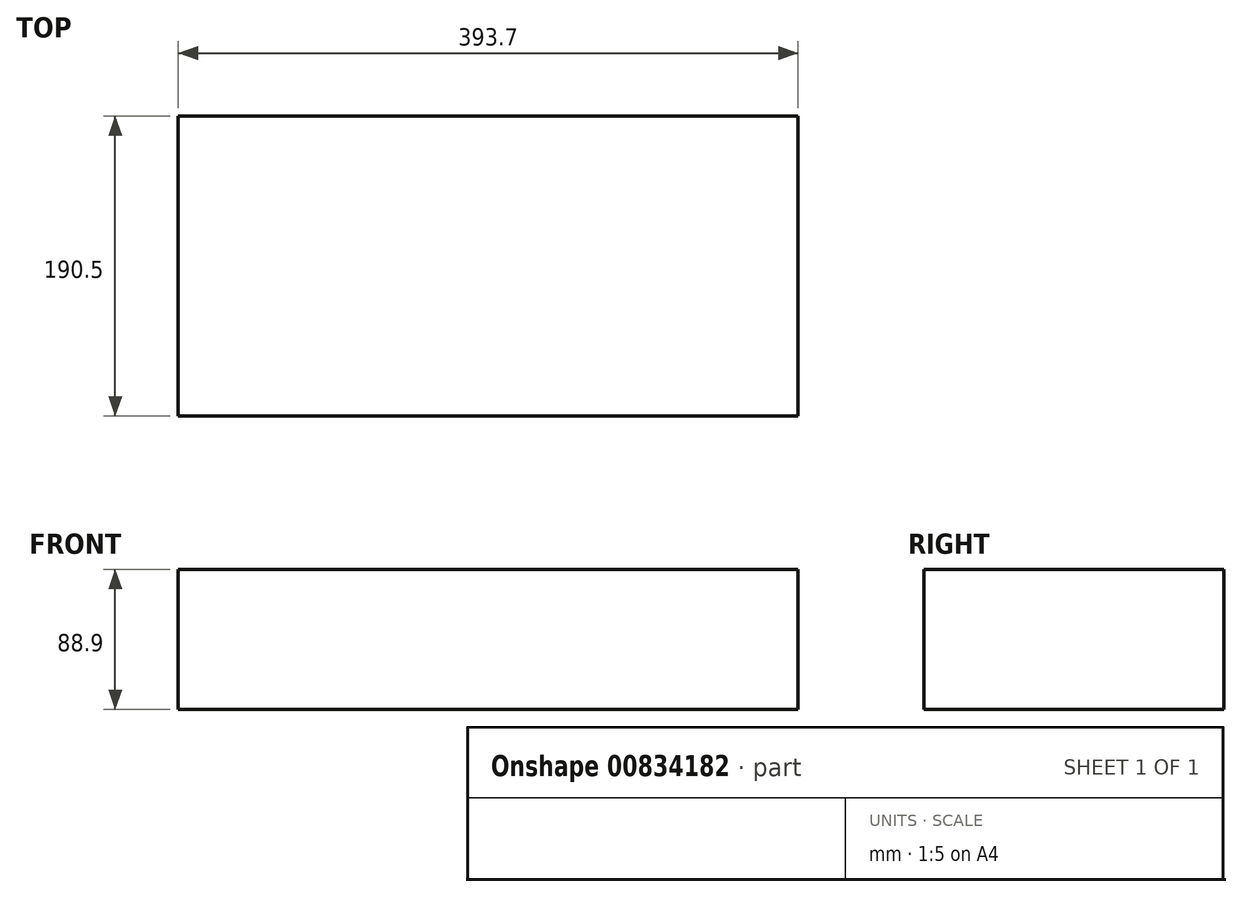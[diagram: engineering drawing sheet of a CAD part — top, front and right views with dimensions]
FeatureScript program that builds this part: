
annotation { "Feature Type Name" : "Feature", "Feature Type Description" : "" }
export const myFeature = defineFeature(function(context is Context, id is Id, definition is map)
    precondition{}
    {
        {
            var Q0;
            Q0=qCreatedBy(makeId("Top.planeOp"),FACE);
            var sketch = newSketch(context, id + "F0", { "sketchPlane" : qUnion([Q0])});
            skLineSegment(sketch, "E0.bottom", {"start": v(-196.85, 95.25) * mm, "end": v(196.85, 95.25) * mm});
            skLineSegment(sketch, "E0.top", {"start": v(-196.85, -95.25) * mm, "end": v(196.85, -95.25) * mm});
            skLineSegment(sketch, "E0.left", {"start": v(-196.85, 95.25) * mm, "end": v(-196.85, -95.25) * mm});
            skLineSegment(sketch, "E0.right", {"start": v(196.85, 95.25) * mm, "end": v(196.85, -95.25) * mm});
            skPoint(sketch, "E0.middle", {"position": v(0, 0) * mm});
            skSolve(sketch);
        }
        {
            var Q0;
            Q0=makeQuery(id+"F0.imprint","IMPRINT",FACE,{"disambiguationData":[TD([[makeQuery(id+"F0.imprint","IMPRINT",EDGE,{"derivedFrom":sQuery(id+"F0.wireOp",EDGE,"E0.bottom")}),-1.0]])]});
            extrude(context, id + "F1", {"entities" : qUnion([Q0]), "depth" : 88.9 * mm, "offsetDistance" : 25.4 * mm});
        }
    });
